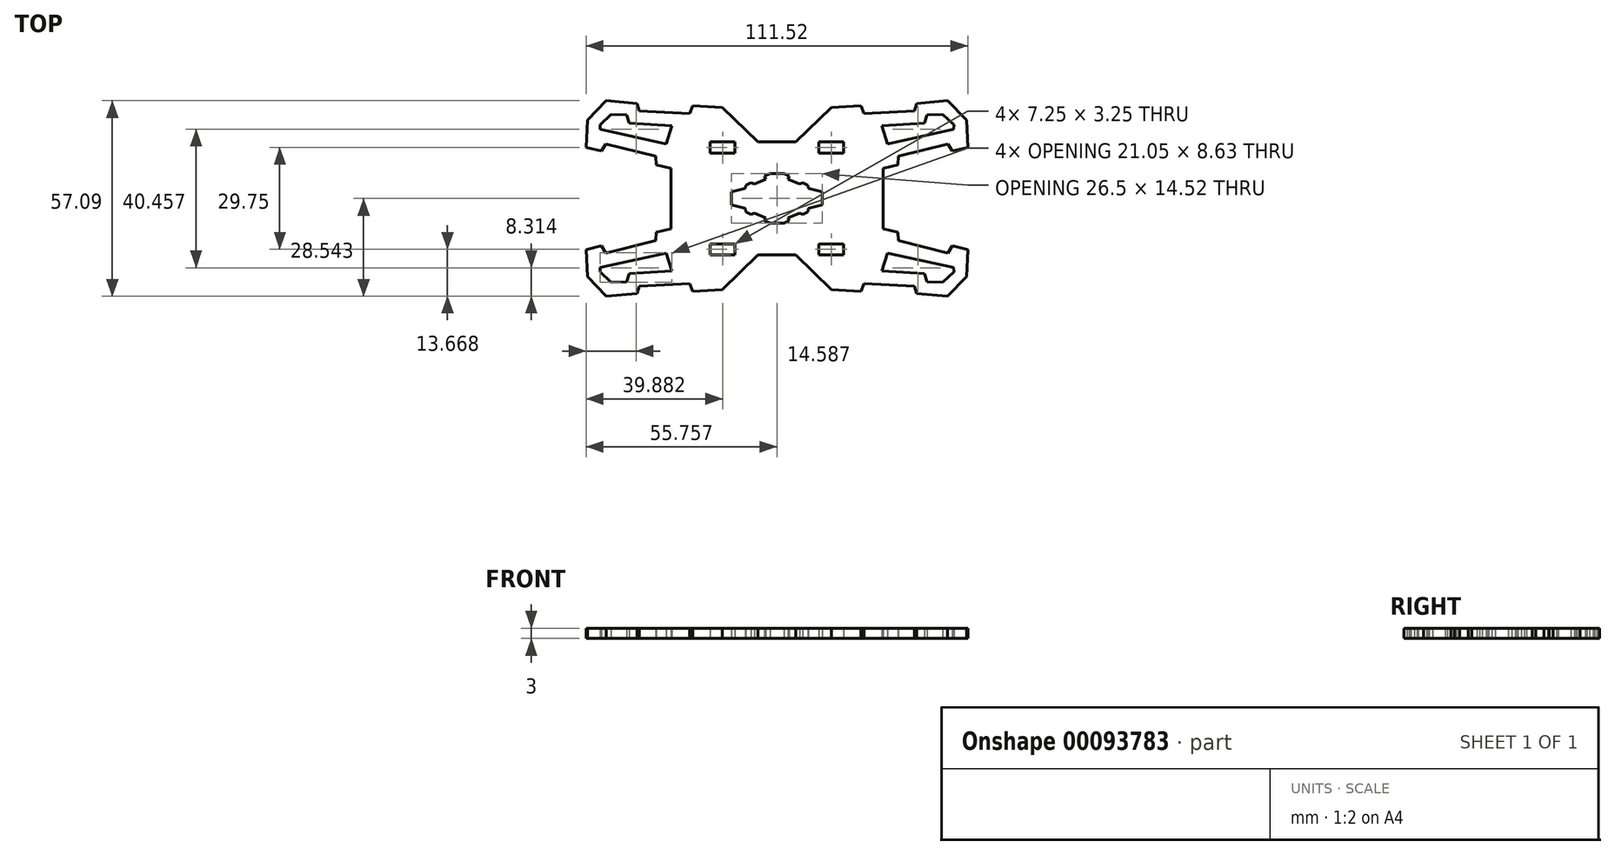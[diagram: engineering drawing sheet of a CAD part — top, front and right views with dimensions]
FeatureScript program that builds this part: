
annotation { "Feature Type Name" : "Feature", "Feature Type Description" : "" }
export const myFeature = defineFeature(function(context is Context, id is Id, definition is map)
    precondition{}
    {
        {
            var Q0;
            Q0=qCreatedBy(makeId("Top.planeOp"),FACE);
            var sketch = newSketch(context, id + "F0", { "sketchPlane" : qUnion([Q0])});
            skPoint(sketch, "E0", {"position": v(-35.95, 42.11) * mm});
            skPoint(sketch, "E1", {"position": v(54.05, 42.69) * mm});
            skLineSegment(sketch, "E2", {"start": v(-15.45, 28.18) * mm, "end": v(23.55, 28.18) * mm, "construction": true});
            skLineSegment(sketch, "E3", {"start": v(4.05, 28.18) * mm, "end": v(4.05, -5.82) * mm, "construction": true});
            skLineSegment(sketch, "E4", {"start": v(4.05, 28.18) * mm, "end": v(-1.49, 28.18) * mm});
            skLineSegment(sketch, "E5", {"start": v(-1.49, 28.18) * mm, "end": v(-11.92, 38.3) * mm});
            skLineSegment(sketch, "E6", {"start": v(-11.92, 38.3) * mm, "end": v(-20.55, 38.81) * mm});
            skLineSegment(sketch, "E7", {"start": v(-20.55, 38.81) * mm, "end": v(-21.45, 36.5) * mm});
            skLineSegment(sketch, "E8", {"start": v(-21.45, 36.5) * mm, "end": v(-36.13, 37.27) * mm});
            skLineSegment(sketch, "E9", {"start": v(-36.13, 37.27) * mm, "end": v(-36.78, 39.46) * mm});
            skLineSegment(sketch, "E10", {"start": v(-36.78, 39.46) * mm, "end": v(-45.8, 40.23) * mm});
            skLineSegment(sketch, "E11", {"start": v(-45.8, 40.23) * mm, "end": v(-51.33, 34.56) * mm});
            skLineSegment(sketch, "E12", {"start": v(-51.33, 34.56) * mm, "end": v(-51.71, 26.58) * mm});
            skLineSegment(sketch, "E13", {"start": v(-51.71, 26.58) * mm, "end": v(-47.2, 25.55) * mm});
            skLineSegment(sketch, "E14", {"start": v(-47.2, 25.55) * mm, "end": v(-45.92, 27.6) * mm});
            skLineSegment(sketch, "E15", {"start": v(-45.92, 27.6) * mm, "end": v(-31.37, 24) * mm});
            skLineSegment(sketch, "E16", {"start": v(-31.37, 24) * mm, "end": v(-31.24, 21.55) * mm});
            skLineSegment(sketch, "E17", {"start": v(-26.95, 20.52) * mm, "end": v(-31.24, 21.55) * mm});
            skLineSegment(sketch, "E18.bottom", {"start": v(-15.45, 28.18) * mm, "end": v(-8.2, 28.18) * mm});
            skLineSegment(sketch, "E18.top", {"start": v(-15.45, 24.93) * mm, "end": v(-8.2, 24.93) * mm});
            skLineSegment(sketch, "E18.left", {"start": v(-15.45, 28.18) * mm, "end": v(-15.45, 24.93) * mm});
            skLineSegment(sketch, "E18.right", {"start": v(-8.2, 28.18) * mm, "end": v(-8.2, 24.93) * mm});
            skLineSegment(sketch, "E19.MirrorCS", {"start": v(4.05, 28.18) * mm, "end": v(9.58, 28.18) * mm});
            skLineSegment(sketch, "E20.MirrorCS", {"start": v(9.58, 28.18) * mm, "end": v(20.01, 38.3) * mm});
            skLineSegment(sketch, "E21.MirrorCS", {"start": v(20.01, 38.3) * mm, "end": v(28.64, 38.81) * mm});
            skLineSegment(sketch, "E22.MirrorCS", {"start": v(28.64, 38.81) * mm, "end": v(29.54, 36.5) * mm});
            skLineSegment(sketch, "E23.MirrorCS", {"start": v(29.54, 36.5) * mm, "end": v(44.23, 37.27) * mm});
            skLineSegment(sketch, "E24.MirrorCS", {"start": v(44.23, 37.27) * mm, "end": v(44.87, 39.46) * mm});
            skLineSegment(sketch, "E25.MirrorCS", {"start": v(44.87, 39.46) * mm, "end": v(53.88, 40.23) * mm});
            skLineSegment(sketch, "E26.MirrorCS", {"start": v(53.88, 40.23) * mm, "end": v(59.42, 34.56) * mm});
            skLineSegment(sketch, "E27.MirrorCS", {"start": v(59.42, 34.56) * mm, "end": v(59.8, 26.58) * mm});
            skLineSegment(sketch, "E28.MirrorCS", {"start": v(59.8, 26.58) * mm, "end": v(55.3, 25.55) * mm});
            skLineSegment(sketch, "E29.MirrorCS", {"start": v(55.3, 25.55) * mm, "end": v(54.01, 27.6) * mm});
            skLineSegment(sketch, "E30.MirrorCS", {"start": v(54.01, 27.6) * mm, "end": v(39.46, 24) * mm});
            skLineSegment(sketch, "E31.MirrorCS", {"start": v(39.46, 24) * mm, "end": v(39.33, 21.55) * mm});
            skLineSegment(sketch, "E32.MirrorCS", {"start": v(35.05, 20.52) * mm, "end": v(39.33, 21.55) * mm});
            skPoint(sketch, "E33", {"position": v(4.05, 11.18) * mm});
            skPoint(sketch, "E34", {"position": v(4.05, 11.68) * mm});
            skLineSegment(sketch, "E35", {"start": v(4.05, 11.68) * mm, "end": v(-39.73, 11.68) * mm});
            skLineSegment(sketch, "E36.MirrorCS", {"start": v(-26.95, 2.84) * mm, "end": v(-31.24, 1.81) * mm});
            skLineSegment(sketch, "E37.MirrorCS", {"start": v(-45.92, -4.24) * mm, "end": v(-31.37, -0.64) * mm});
            skLineSegment(sketch, "E38.MirrorCS", {"start": v(-47.2, -2.18) * mm, "end": v(-45.92, -4.24) * mm});
            skLineSegment(sketch, "E39.MirrorCS", {"start": v(-51.71, -3.21) * mm, "end": v(-47.2, -2.18) * mm});
            skLineSegment(sketch, "E40.MirrorCS", {"start": v(-51.33, -11.2) * mm, "end": v(-51.71, -3.21) * mm});
            skLineSegment(sketch, "E41.MirrorCS", {"start": v(-45.8, -16.86) * mm, "end": v(-51.33, -11.2) * mm});
            skLineSegment(sketch, "E42.MirrorCS", {"start": v(-36.78, -16.09) * mm, "end": v(-45.8, -16.86) * mm});
            skLineSegment(sketch, "E43.MirrorCS", {"start": v(-36.13, -13.9) * mm, "end": v(-36.78, -16.09) * mm});
            skLineSegment(sketch, "E44.MirrorCS", {"start": v(-21.45, -13.13) * mm, "end": v(-36.13, -13.9) * mm});
            skLineSegment(sketch, "E45.MirrorCS", {"start": v(-20.55, -15.45) * mm, "end": v(-21.45, -13.13) * mm});
            skLineSegment(sketch, "E46.MirrorCS", {"start": v(-11.92, -14.93) * mm, "end": v(-20.55, -15.45) * mm});
            skLineSegment(sketch, "E47.MirrorCS", {"start": v(-1.49, -4.82) * mm, "end": v(-11.92, -14.93) * mm});
            skLineSegment(sketch, "E48.MirrorCS", {"start": v(4.05, -4.82) * mm, "end": v(-1.49, -4.82) * mm});
            skLineSegment(sketch, "E49.MirrorCS", {"start": v(4.05, -4.82) * mm, "end": v(9.58, -4.82) * mm});
            skLineSegment(sketch, "E50.MirrorCS", {"start": v(9.58, -4.82) * mm, "end": v(20.01, -14.93) * mm});
            skLineSegment(sketch, "E51.MirrorCS", {"start": v(20.01, -14.93) * mm, "end": v(28.64, -15.45) * mm});
            skLineSegment(sketch, "E52.MirrorCS", {"start": v(29.54, -13.13) * mm, "end": v(44.23, -13.9) * mm});
            skLineSegment(sketch, "E53.MirrorCS", {"start": v(28.64, -15.45) * mm, "end": v(29.54, -13.13) * mm});
            skLineSegment(sketch, "E54.MirrorCS", {"start": v(44.23, -13.9) * mm, "end": v(44.87, -16.09) * mm});
            skLineSegment(sketch, "E55.MirrorCS", {"start": v(44.87, -16.09) * mm, "end": v(53.88, -16.86) * mm});
            skLineSegment(sketch, "E56.MirrorCS", {"start": v(53.88, -16.86) * mm, "end": v(59.42, -11.2) * mm});
            skLineSegment(sketch, "E57.MirrorCS", {"start": v(59.42, -11.2) * mm, "end": v(59.8, -3.21) * mm});
            skLineSegment(sketch, "E58.MirrorCS", {"start": v(59.8, -3.21) * mm, "end": v(55.3, -2.18) * mm});
            skLineSegment(sketch, "E59.MirrorCS", {"start": v(55.3, -2.18) * mm, "end": v(54.01, -4.24) * mm});
            skLineSegment(sketch, "E60.MirrorCS", {"start": v(54.01, -4.24) * mm, "end": v(39.46, -0.64) * mm});
            skLineSegment(sketch, "E61.MirrorCS", {"start": v(39.46, -0.64) * mm, "end": v(39.33, 1.81) * mm});
            skLineSegment(sketch, "E62.MirrorCS", {"start": v(35.05, 2.84) * mm, "end": v(39.33, 1.81) * mm});
            skLineSegment(sketch, "E63.MirrorCS", {"start": v(-31.37, -0.64) * mm, "end": v(-31.24, 1.81) * mm});
            skLineSegment(sketch, "E64.MirrorCS", {"start": v(-15.45, -4.82) * mm, "end": v(-8.2, -4.82) * mm});
            skLineSegment(sketch, "E65.MirrorCS", {"start": v(-15.45, -4.82) * mm, "end": v(-15.45, -1.57) * mm});
            skLineSegment(sketch, "E66.MirrorCS", {"start": v(-8.2, -4.82) * mm, "end": v(-8.2, -1.57) * mm});
            skLineSegment(sketch, "E67.MirrorCS", {"start": v(-15.45, -1.57) * mm, "end": v(-8.2, -1.57) * mm});
            skLineSegment(sketch, "E68.MirrorCS", {"start": v(16.3, 28.18) * mm, "end": v(16.3, 24.93) * mm});
            skLineSegment(sketch, "E69.MirrorCS", {"start": v(23.55, 28.18) * mm, "end": v(16.3, 28.18) * mm});
            skLineSegment(sketch, "E70.MirrorCS", {"start": v(23.55, 28.18) * mm, "end": v(23.55, 24.93) * mm});
            skLineSegment(sketch, "E71.MirrorCS", {"start": v(23.55, 24.93) * mm, "end": v(16.3, 24.93) * mm});
            skLineSegment(sketch, "E72.MirrorCS", {"start": v(23.55, -1.57) * mm, "end": v(16.3, -1.57) * mm});
            skLineSegment(sketch, "E73.MirrorCS", {"start": v(23.55, -4.82) * mm, "end": v(23.55, -1.57) * mm});
            skLineSegment(sketch, "E74.MirrorCS", {"start": v(23.55, -4.82) * mm, "end": v(16.3, -4.82) * mm});
            skLineSegment(sketch, "E75.MirrorCS", {"start": v(16.3, -4.82) * mm, "end": v(16.3, -1.57) * mm});
            skLineSegment(sketch, "E76", {"start": v(-28.3, 27.6) * mm, "end": v(-47.59, 31.88) * mm});
            skLineSegment(sketch, "E77", {"start": v(-47.59, 31.88) * mm, "end": v(-47.65, 33.13) * mm});
            skLineSegment(sketch, "E78", {"start": v(-47.65, 33.13) * mm, "end": v(-44.39, 36.23) * mm});
            skLineSegment(sketch, "E79", {"start": v(-44.39, 36.23) * mm, "end": v(-39.86, 36.06) * mm});
            skLineSegment(sketch, "E80", {"start": v(-39.86, 36.06) * mm, "end": v(-39.03, 33.69) * mm});
            skLineSegment(sketch, "E81", {"start": v(-39.03, 33.69) * mm, "end": v(-26.6, 32.91) * mm});
            skLineSegment(sketch, "E82", {"start": v(-26.6, 32.91) * mm, "end": v(-28.3, 27.6) * mm});
            skLineSegment(sketch, "E83.MirrorCS", {"start": v(-28.3, -4.23) * mm, "end": v(-47.59, -8.52) * mm});
            skLineSegment(sketch, "E84.MirrorCS", {"start": v(-47.59, -8.52) * mm, "end": v(-47.65, -9.77) * mm});
            skLineSegment(sketch, "E85.MirrorCS", {"start": v(-47.65, -9.77) * mm, "end": v(-44.39, -12.86) * mm});
            skLineSegment(sketch, "E86.MirrorCS", {"start": v(-44.39, -12.86) * mm, "end": v(-39.86, -12.7) * mm});
            skLineSegment(sketch, "E87.MirrorCS", {"start": v(-39.86, -12.7) * mm, "end": v(-39.03, -10.32) * mm});
            skLineSegment(sketch, "E88.MirrorCS", {"start": v(-39.03, -10.32) * mm, "end": v(-26.6, -9.55) * mm});
            skLineSegment(sketch, "E89.MirrorCS", {"start": v(-26.6, -9.55) * mm, "end": v(-28.3, -4.23) * mm});
            skLineSegment(sketch, "E90.MirrorCS", {"start": v(4.05, -4.82) * mm, "end": v(4.05, 29.18) * mm, "construction": true});
            skLineSegment(sketch, "E91.MirrorCS", {"start": v(36.4, -4.23) * mm, "end": v(55.68, -8.52) * mm});
            skLineSegment(sketch, "E92.MirrorCS", {"start": v(34.7, -9.55) * mm, "end": v(36.4, -4.23) * mm});
            skLineSegment(sketch, "E93.MirrorCS", {"start": v(47.12, -10.32) * mm, "end": v(34.7, -9.55) * mm});
            skLineSegment(sketch, "E94.MirrorCS", {"start": v(47.95, -12.7) * mm, "end": v(47.12, -10.32) * mm});
            skLineSegment(sketch, "E95.MirrorCS", {"start": v(52.48, -12.86) * mm, "end": v(47.95, -12.7) * mm});
            skLineSegment(sketch, "E96.MirrorCS", {"start": v(55.74, -9.77) * mm, "end": v(52.48, -12.86) * mm});
            skLineSegment(sketch, "E97.MirrorCS", {"start": v(55.68, -8.52) * mm, "end": v(55.74, -9.77) * mm});
            skLineSegment(sketch, "E98", {"start": v(-26.95, 20.52) * mm, "end": v(-26.95, 2.84) * mm});
            skLineSegment(sketch, "E99", {"start": v(35.05, 2.84) * mm, "end": v(35.05, 20.52) * mm});
            skLineSegment(sketch, "E100.MirrorCS", {"start": v(34.7, 32.91) * mm, "end": v(36.4, 27.6) * mm});
            skLineSegment(sketch, "E101.MirrorCS", {"start": v(47.12, 33.69) * mm, "end": v(34.7, 32.91) * mm});
            skLineSegment(sketch, "E102.MirrorCS", {"start": v(36.4, 27.6) * mm, "end": v(55.68, 31.88) * mm});
            skLineSegment(sketch, "E103.MirrorCS", {"start": v(47.95, 36.06) * mm, "end": v(47.12, 33.69) * mm});
            skLineSegment(sketch, "E104.MirrorCS", {"start": v(52.48, 36.23) * mm, "end": v(47.95, 36.06) * mm});
            skLineSegment(sketch, "E105.MirrorCS", {"start": v(55.74, 33.13) * mm, "end": v(52.48, 36.23) * mm});
            skLineSegment(sketch, "E106.MirrorCS", {"start": v(55.68, 31.88) * mm, "end": v(55.74, 33.13) * mm});
            skLineSegment(sketch, "E107", {"start": v(4.05, 18.94) * mm, "end": v(2.01, 18.94) * mm});
            skLineSegment(sketch, "E108", {"start": v(2.01, 18.94) * mm, "end": v(0.43, 18.2) * mm});
            skLineSegment(sketch, "E109", {"start": v(0.43, 18.2) * mm, "end": v(0.8, 17.36) * mm});
            skLineSegment(sketch, "E110", {"start": v(0.8, 17.36) * mm, "end": v(-2.58, 15.93) * mm});
            skLineSegment(sketch, "E111", {"start": v(-2.58, 15.93) * mm, "end": v(-3.48, 16.31) * mm});
            skLineSegment(sketch, "E112", {"start": v(-3.48, 16.31) * mm, "end": v(-5.06, 15.56) * mm});
            skLineSegment(sketch, "E113", {"start": v(-5.06, 15.56) * mm, "end": v(-5.14, 14.58) * mm});
            skLineSegment(sketch, "E114", {"start": v(-5.14, 14.58) * mm, "end": v(-9.2, 13.6) * mm});
            skLineSegment(sketch, "E115", {"start": v(-9.2, 13.6) * mm, "end": v(-9.2, 11.68) * mm});
            skLineSegment(sketch, "E116.MirrorCS", {"start": v(4.05, 18.94) * mm, "end": v(6.08, 18.94) * mm});
            skLineSegment(sketch, "E117.MirrorCS", {"start": v(6.08, 18.94) * mm, "end": v(7.66, 18.2) * mm});
            skLineSegment(sketch, "E118.MirrorCS", {"start": v(7.66, 18.2) * mm, "end": v(7.29, 17.36) * mm});
            skLineSegment(sketch, "E119.MirrorCS", {"start": v(7.29, 17.36) * mm, "end": v(10.67, 15.93) * mm});
            skLineSegment(sketch, "E120.MirrorCS", {"start": v(10.67, 15.93) * mm, "end": v(11.58, 16.31) * mm});
            skLineSegment(sketch, "E121.MirrorCS", {"start": v(11.58, 16.31) * mm, "end": v(13.16, 15.56) * mm});
            skLineSegment(sketch, "E122.MirrorCS", {"start": v(13.16, 15.56) * mm, "end": v(13.23, 14.58) * mm});
            skLineSegment(sketch, "E123.MirrorCS", {"start": v(13.23, 14.58) * mm, "end": v(17.3, 13.6) * mm});
            skLineSegment(sketch, "E124.MirrorCS", {"start": v(17.3, 13.6) * mm, "end": v(17.3, 11.68) * mm});
            skLineSegment(sketch, "E125.MirrorCS", {"start": v(-3.48, 7.05) * mm, "end": v(-5.06, 7.8) * mm});
            skLineSegment(sketch, "E126.MirrorCS", {"start": v(-5.14, 8.79) * mm, "end": v(-9.2, 9.76) * mm});
            skLineSegment(sketch, "E127.MirrorCS", {"start": v(2.01, 4.42) * mm, "end": v(0.43, 5.17) * mm});
            skLineSegment(sketch, "E128.MirrorCS", {"start": v(0.43, 5.17) * mm, "end": v(0.8, 6) * mm});
            skLineSegment(sketch, "E129.MirrorCS", {"start": v(0.8, 6) * mm, "end": v(-2.58, 7.43) * mm});
            skLineSegment(sketch, "E130.MirrorCS", {"start": v(-5.06, 7.8) * mm, "end": v(-5.14, 8.79) * mm});
            skLineSegment(sketch, "E131.MirrorCS", {"start": v(-2.58, 7.43) * mm, "end": v(-3.48, 7.05) * mm});
            skLineSegment(sketch, "E132.MirrorCS", {"start": v(-9.2, 9.76) * mm, "end": v(-9.2, 11.68) * mm});
            skLineSegment(sketch, "E133.MirrorCS", {"start": v(4.05, 4.42) * mm, "end": v(2.01, 4.42) * mm});
            skLineSegment(sketch, "E134.MirrorCS", {"start": v(11.58, 7.05) * mm, "end": v(13.16, 7.8) * mm});
            skLineSegment(sketch, "E135.MirrorCS", {"start": v(10.67, 7.43) * mm, "end": v(11.58, 7.05) * mm});
            skLineSegment(sketch, "E136.MirrorCS", {"start": v(13.16, 7.8) * mm, "end": v(13.23, 8.79) * mm});
            skLineSegment(sketch, "E137.MirrorCS", {"start": v(7.66, 5.17) * mm, "end": v(7.29, 6) * mm});
            skLineSegment(sketch, "E138.MirrorCS", {"start": v(7.29, 6) * mm, "end": v(10.67, 7.43) * mm});
            skLineSegment(sketch, "E139.MirrorCS", {"start": v(6.08, 4.42) * mm, "end": v(7.66, 5.17) * mm});
            skLineSegment(sketch, "E140.MirrorCS", {"start": v(13.23, 8.79) * mm, "end": v(17.3, 9.76) * mm});
            skLineSegment(sketch, "E141.MirrorCS", {"start": v(4.05, 4.42) * mm, "end": v(6.08, 4.42) * mm});
            skLineSegment(sketch, "E142.MirrorCS", {"start": v(17.3, 9.76) * mm, "end": v(17.3, 11.68) * mm});
            skSolve(sketch);
        }
        {
            var Q0;
            Q0=makeQuery(id+"F0.imprint","IMPRINT",FACE,{"disambiguationData":[TD([[makeQuery(id+"F0.imprint","IMPRINT",EDGE,{"derivedFrom":sQuery(id+"F0.wireOp",EDGE,"E4")}),1.0]])]});
            extrude(context, id + "F1", {"entities" : qUnion([Q0]), "depth" : 3 * mm});
        }
    });
